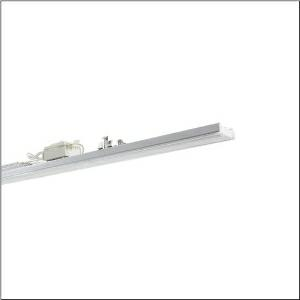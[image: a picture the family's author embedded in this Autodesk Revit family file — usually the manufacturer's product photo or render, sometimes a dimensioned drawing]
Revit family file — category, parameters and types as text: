
# Revit family: licross_r__21_recessed_mo_52tl10dn4axg_1c07
name_source: partatom
category: Lighting Fixtures
units: mm (PartAtom-declared; Revit-internal decimal feet)

## family parameters
Cut with Voids When Loaded = No
Host = Face
Light Source = No
Part Type = Normal
Room Calculation Point = No
Round Connector Dimension = Use Diameter
Shared = No

## types (1)
- --- (1 x LED, 10000 lm, 58 W, 4000K)
    Apparent Load = 58 VA
    CIE Flux Codes = 50 81 96 100 100
    Color Rendering = 80
    Color Temperature = 4000K
    Default Elevation = 1800 mm
    Description = Licross® 21 Recessed MO, luminaire insert, of sheet steel, galvanised, coil coated, white, length: 1.500mm, width: 66mm, height: 67mm, LED rated luminous flux: 10.000lm, light colour: 840, control gear: DALI 2, with plug, 5-pole, with phase selection, mains connection: 220..240V, AC, 50/60Hz, rated input power: 58W, halogen-free wiring, primary optical cover: cover, of PMMA, light emission: direct distribution, primary light characteristic: symmetric, protection rating (complete): IP40, insulation class (complete): insulation class I (protective earthing), certification: CE, ENEC, VDE, UKCA, protection symbol: D if used in an environment without relevant dust loads with corresponding accessories, impact resistance: IK06, permissible ambient temperature for indoor applications: -25..+35°C, corresponds to IFS (International Featured Standards) requirements for safety and quality in the food industry, reducing of maximum allowable ambient temperature of 5°C with ceiling mounting, LABS conformity tested according to VDMA 24364:2018-05, packaging unit: 1 piece
    Height = 58 mm
    Lamp = 1 x LED
    Lamp Light Flux = 10000 lm
    Lamp Power = 58 W
    Lamp count = 1
    Length = 1500 mm
    Luminous efficacy = 172 lm/W
    Manufacturer = Siteco
    ModVariant = No
    Model = 52TL10DN4AXG
    Mounting Place = Ceiling
    Mounting Type = Pendant
    Number of Poles = 1
    OnlyDefault = Yes
    Power Factor = 1
    Product Name = Licross® 21 Recessed MO
    Product group = luminaire insert
    ProductGroupID = 902
    Protection Class = Protection class I
    Protection Degree = IP 40
    RLX_Detail_Level = 1
    RLX_Emergency_Light_Flux = 0 lm
    RLX_Emergency_Type = 0
    RLX_Emergency_Type_DB = No
    RlxData = <blob elided: 24333 chars, md5=9e434589>
    Socket = socket
    Standby Power = 0 W
    System Light Flux = 10000 lm
    System Power = 58 W
    Type Comments = factory setting: luminous flux: 100 % | dim-lin: 254 | 390 mA
    Type Image = l_1296930.jpg
    URL = http://relux.com
    VarID = @adj_127550
    Voltage = 0 V
    Weight = 0.00 kg
    Width = 66 mm

## geometry (parser evidence)
native form markers: Blend x4, Sweep x11
no freeform markers — native parametric forms only
